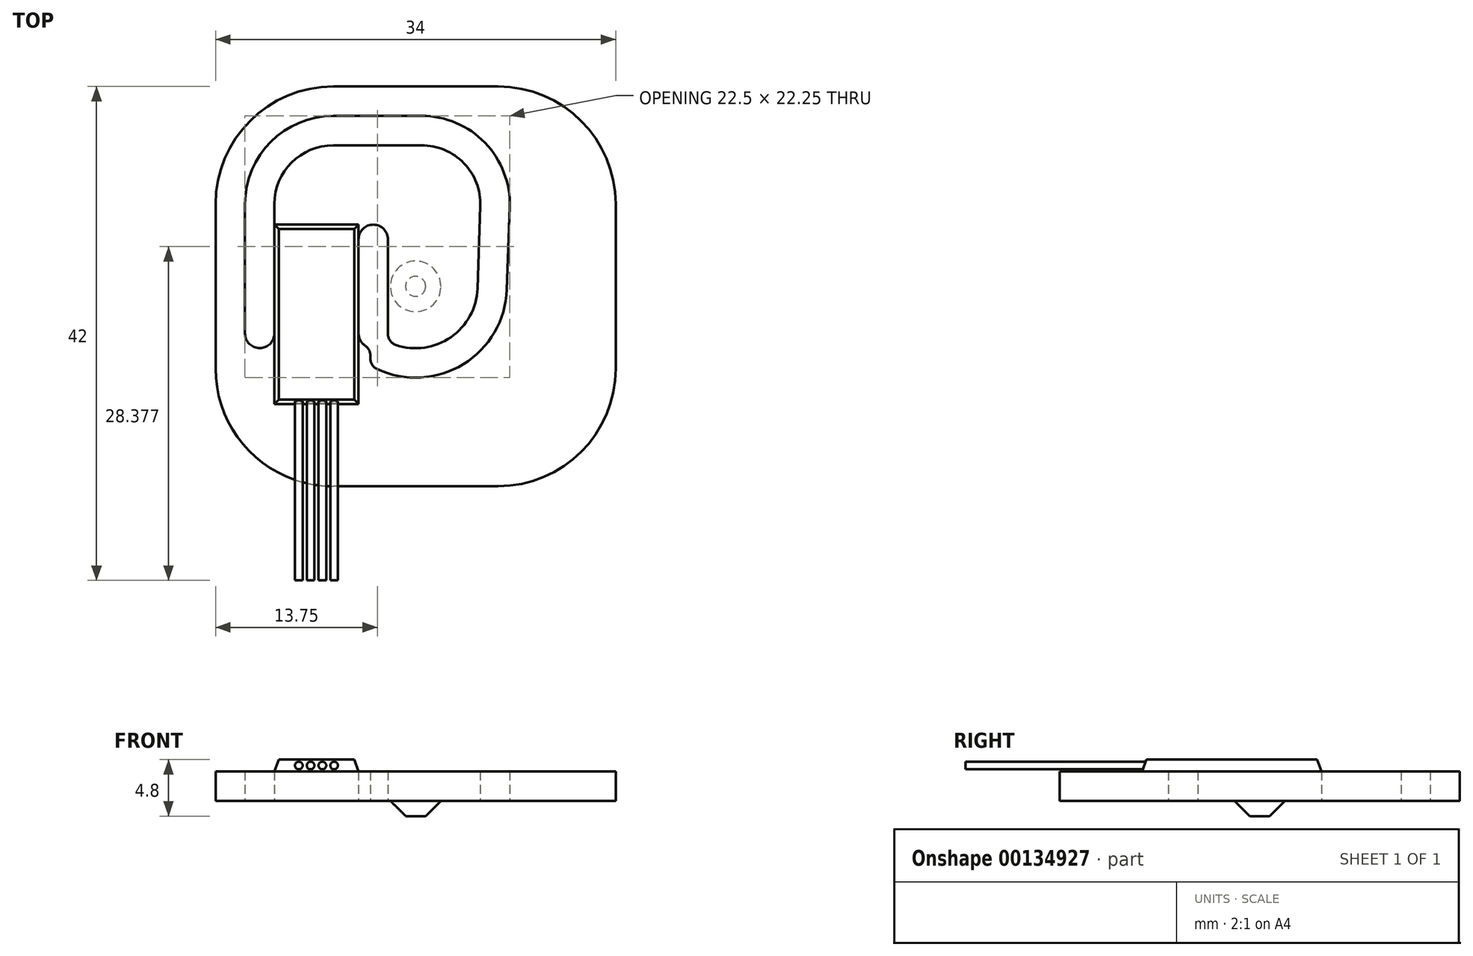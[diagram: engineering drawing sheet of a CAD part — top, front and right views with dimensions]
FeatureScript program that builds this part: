
annotation { "Feature Type Name" : "Feature", "Feature Type Description" : "" }
export const myFeature = defineFeature(function(context is Context, id is Id, definition is map)
    precondition{}
    {
        {
            var Q0;
            Q0=qCreatedBy(makeId("Top.planeOp"),FACE);
            var sketch = newSketch(context, id + "F0", { "sketchPlane" : qUnion([Q0])});
            skLineSegment(sketch, "E0.bottom", {"start": v(7, -17) * mm, "end": v(-7, -17) * mm});
            skLineSegment(sketch, "E0.top", {"start": v(7, 17) * mm, "end": v(-7, 17) * mm});
            skLineSegment(sketch, "E0.left", {"start": v(17, -7) * mm, "end": v(17, 7) * mm});
            skLineSegment(sketch, "E0.right", {"start": v(-17, -7) * mm, "end": v(-17, 7) * mm});
            skPoint(sketch, "E0.middle", {"position": v(0, 0) * mm});
            skPoint(sketch, "E1.visualSharp", {"position": v(-17, 17) * mm});
            skArc(sketch, "E1.filletArc", {"start": v(-7, 17) * mm, "mid": v(-14.07, 14.07) * mm, "end": v(-17, 7) * mm});
            skPoint(sketch, "E2.visualSharp", {"position": v(17, 17) * mm});
            skArc(sketch, "E2.filletArc", {"start": v(17, 7) * mm, "mid": v(14.07, 14.07) * mm, "end": v(7, 17) * mm});
            skPoint(sketch, "E3.visualSharp", {"position": v(17, -17) * mm});
            skArc(sketch, "E3.filletArc", {"start": v(7, -17) * mm, "mid": v(14.07, -14.07) * mm, "end": v(17, -7) * mm});
            skPoint(sketch, "E4.visualSharp", {"position": v(-17, -17) * mm});
            skArc(sketch, "E4.filletArc", {"start": v(-17, -7) * mm, "mid": v(-14.07, -14.07) * mm, "end": v(-7, -17) * mm});
            skLineSegment(sketch, "E5.0", {"start": v(0.5, 14.5) * mm, "end": v(-7, 14.5) * mm});
            skArc(sketch, "E5.1", {"start": v(-7, 14.5) * mm, "mid": v(-12.3, 12.3) * mm, "end": v(-14.5, 7) * mm});
            skLineSegment(sketch, "E5.2", {"start": v(-14.5, -4) * mm, "end": v(-14.5, 7) * mm});
            skArc(sketch, "E6", {"start": v(8, 6.74) * mm, "mid": v(5.9, 12.2) * mm, "end": v(0.5, 14.5) * mm});
            skLineSegment(sketch, "E7", {"start": v(8, 6.74) * mm, "end": v(7.76, -0.27) * mm});
            skArc(sketch, "E8", {"start": v(-3.27, -7.04) * mm, "mid": v(4.06, -6.61) * mm, "end": v(7.76, -0.27) * mm});
            skArc(sketch, "E9.0", {"start": v(-1.67, -4.99) * mm, "mid": v(3, -4.32) * mm, "end": v(5.26, -0.18) * mm});
            skLineSegment(sketch, "E9.1", {"start": v(5.5, 6.83) * mm, "end": v(5.26, -0.18) * mm});
            skLineSegment(sketch, "E9.2", {"start": v(-12, -4) * mm, "end": v(-12, 7) * mm});
            skArc(sketch, "E9.3", {"start": v(-7, 12) * mm, "mid": v(-10.54, 10.54) * mm, "end": v(-12, 7) * mm});
            skLineSegment(sketch, "E9.4", {"start": v(0.5, 12) * mm, "end": v(-7, 12) * mm});
            skArc(sketch, "E9.5", {"start": v(5.5, 6.83) * mm, "mid": v(4.1, 10.47) * mm, "end": v(0.5, 12) * mm});
            skArc(sketch, "E10", {"start": v(-14.5, -4) * mm, "mid": v(-13.25, -5.25) * mm, "end": v(-12, -4) * mm});
            skLineSegment(sketch, "E11", {"start": v(-2.35, -4.04) * mm, "end": v(-2.35, 4) * mm});
            skArc(sketch, "E12", {"start": v(-2.35, 4) * mm, "mid": v(-3.6, 5.25) * mm, "end": v(-4.85, 4) * mm});
            skLineSegment(sketch, "E13", {"start": v(-4.85, 4) * mm, "end": v(-4.85, -4) * mm});
            skArc(sketch, "E14", {"start": v(-4.85, -4) * mm, "mid": v(-4.7, -4.59) * mm, "end": v(-4.3, -5.04) * mm});
            skLineSegment(sketch, "E15", {"start": v(-3.85, -5.87) * mm, "end": v(-3.85, -6.13) * mm});
            skPoint(sketch, "E16.visualSharp", {"position": v(-3.85, -5.22) * mm});
            skArc(sketch, "E16.filletArc", {"start": v(-3.85, -5.87) * mm, "mid": v(-3.97, -5.4) * mm, "end": v(-4.3, -5.04) * mm});
            skPoint(sketch, "E17.visualSharp", {"position": v(-3.85, -6.74) * mm});
            skArc(sketch, "E17.filletArc", {"start": v(-3.85, -6.13) * mm, "mid": v(-3.7, -6.67) * mm, "end": v(-3.27, -7.04) * mm});
            skPoint(sketch, "E18.visualSharp", {"position": v(-2.35, -4.7) * mm});
            skArc(sketch, "E18.filletArc", {"start": v(-2.35, -4.04) * mm, "mid": v(-2.16, -4.62) * mm, "end": v(-1.67, -4.99) * mm});
            skSolve(sketch);
        }
        {
            var Q0;
            Q0 = qSketchRegion(id + "F0", true);
            extrude(context, id + "F1", {"entities" : qUnion([Q0]), "depth" : 2.5 * mm});
        }
        {
            var Q0;
            Q0=makeQuery(id+"F1.opExtrude","CAP_FACE",FACE,{"disambiguationData":[OSD([sQuery(id+"F0.wireOp",EDGE,"E0.bottom"),sQuery(id+"F0.wireOp",EDGE,"E0.top"),sQuery(id+"F0.wireOp",EDGE,"E0.left"),sQuery(id+"F0.wireOp",EDGE,"E0.right"),sQuery(id+"F0.wireOp",EDGE,"E1.filletArc"),sQuery(id+"F0.wireOp",EDGE,"E2.filletArc"),sQuery(id+"F0.wireOp",EDGE,"E3.filletArc"),sQuery(id+"F0.wireOp",EDGE,"E4.filletArc"),sQuery(id+"F0.wireOp",EDGE,"E5.0"),sQuery(id+"F0.wireOp",EDGE,"E5.1"),sQuery(id+"F0.wireOp",EDGE,"E5.2"),sQuery(id+"F0.wireOp",EDGE,"E6"),sQuery(id+"F0.wireOp",EDGE,"E7"),sQuery(id+"F0.wireOp",EDGE,"E8"),sQuery(id+"F0.wireOp",EDGE,"E9.0"),sQuery(id+"F0.wireOp",EDGE,"E9.1"),sQuery(id+"F0.wireOp",EDGE,"E9.2"),sQuery(id+"F0.wireOp",EDGE,"E9.3"),sQuery(id+"F0.wireOp",EDGE,"E9.4"),sQuery(id+"F0.wireOp",EDGE,"E9.5"),sQuery(id+"F0.wireOp",EDGE,"E10"),sQuery(id+"F0.wireOp",EDGE,"E11"),sQuery(id+"F0.wireOp",EDGE,"E12"),sQuery(id+"F0.wireOp",EDGE,"E13"),sQuery(id+"F0.wireOp",EDGE,"E14"),sQuery(id+"F0.wireOp",EDGE,"E15"),sQuery(id+"F0.wireOp",EDGE,"E16.filletArc"),sQuery(id+"F0.wireOp",EDGE,"E17.filletArc"),sQuery(id+"F0.wireOp",EDGE,"E18.filletArc")])],"isStart":false});
            var sketch = newSketch(context, id + "F2", { "sketchPlane" : qUnion([Q0])});
            skLineSegment(sketch, "E19.0", {"start": v(-12, -4) * mm, "end": v(-12, 5.25) * mm});
            skLineSegment(sketch, "E20.0", {"start": v(-4.85, 4) * mm, "end": v(-4.85, -4) * mm});
            skLineSegment(sketch, "E21", {"start": v(-4.85, 4) * mm, "end": v(-4.85, 5.25) * mm});
            skLineSegment(sketch, "E22", {"start": v(-4.85, 5.25) * mm, "end": v(-12, 5.25) * mm});
            skLineSegment(sketch, "E23", {"start": v(-12, -4) * mm, "end": v(-12, -10) * mm});
            skLineSegment(sketch, "E24", {"start": v(-12, -10) * mm, "end": v(-4.85, -10) * mm});
            skLineSegment(sketch, "E25", {"start": v(-4.85, -10) * mm, "end": v(-4.85, -4) * mm});
            skPoint(sketch, "E26.orphan", {"position": v(-12, 7) * mm});
            skSolve(sketch);
        }
        {
            var Q0;
            Q0 = qSketchRegion(id + "F2", true);
            extrude(context, id + "F3", {"entities" : qUnion([Q0]), "depth" : 1 * mm, "hasDraft" : true, "draftAngle" : 20 * degree, "draftPullDirection" : true});
        }
        {
            var Q0;
            Q0=qCreatedBy(makeId("Front.planeOp"),FACE);
            var sketch = newSketch(context, id + "F4", { "sketchPlane" : qUnion([Q0])});
            skLineSegment(sketch, "E27.0", {"start": v(-11.64, 3.5) * mm, "end": v(-5.21, 3.5) * mm, "construction": true});
            skLineSegment(sketch, "E28.0", {"start": v(-12, 2.5) * mm, "end": v(-4.85, 2.5) * mm, "construction": true});
            skCircle(sketch, "E29", {"center": v(-9.92, 3) * mm, "radius": 0.33 * mm});
            skCircle(sketch, "E30", {"center": v(-8.92, 3) * mm, "radius": 0.33 * mm});
            skCircle(sketch, "E31", {"center": v(-7.92, 3) * mm, "radius": 0.33 * mm});
            skCircle(sketch, "E32", {"center": v(-6.92, 3) * mm, "radius": 0.33 * mm});
            skLineSegment(sketch, "E33", {"start": v(-9.92, 3) * mm, "end": v(-8.92, 3) * mm, "construction": true});
            skLineSegment(sketch, "E34", {"start": v(-7.92, 3) * mm, "end": v(-6.92, 3) * mm, "construction": true});
            skLineSegment(sketch, "E35", {"start": v(-7.92, 3) * mm, "end": v(-8.92, 3) * mm, "construction": true});
            skLineSegment(sketch, "E36", {"start": v(-8.42, 3) * mm, "end": v(-8.42, 2.5) * mm, "construction": true});
            skPoint(sketch, "E37.orphan", {"position": v(-8.42, 3.5) * mm});
            skLineSegment(sketch, "E38", {"start": v(-8.42, 3) * mm, "end": v(-8.42, 3.5) * mm, "construction": true});
            skSolve(sketch);
        }
        {
            var Q0;
            Q0 = qSketchRegion(id + "F4", true);
            extrude(context, id + "F5", {"entities" : qUnion([Q0]), "operationType" : NewBodyOperationType.ADD, "depth" : 25 * mm});
        }
        {
            var Q0;
            Q0=makeQuery(id+"F1.opExtrude","CAP_FACE",FACE,{"disambiguationData":[OSD([sQuery(id+"F0.wireOp",EDGE,"E0.bottom"),sQuery(id+"F0.wireOp",EDGE,"E0.top"),sQuery(id+"F0.wireOp",EDGE,"E0.left"),sQuery(id+"F0.wireOp",EDGE,"E0.right"),sQuery(id+"F0.wireOp",EDGE,"E1.filletArc"),sQuery(id+"F0.wireOp",EDGE,"E2.filletArc"),sQuery(id+"F0.wireOp",EDGE,"E3.filletArc"),sQuery(id+"F0.wireOp",EDGE,"E4.filletArc"),sQuery(id+"F0.wireOp",EDGE,"E5.0"),sQuery(id+"F0.wireOp",EDGE,"E5.1"),sQuery(id+"F0.wireOp",EDGE,"E5.2"),sQuery(id+"F0.wireOp",EDGE,"E6"),sQuery(id+"F0.wireOp",EDGE,"E7"),sQuery(id+"F0.wireOp",EDGE,"E8"),sQuery(id+"F0.wireOp",EDGE,"E9.0"),sQuery(id+"F0.wireOp",EDGE,"E9.1"),sQuery(id+"F0.wireOp",EDGE,"E9.2"),sQuery(id+"F0.wireOp",EDGE,"E9.3"),sQuery(id+"F0.wireOp",EDGE,"E9.4"),sQuery(id+"F0.wireOp",EDGE,"E9.5"),sQuery(id+"F0.wireOp",EDGE,"E10"),sQuery(id+"F0.wireOp",EDGE,"E11"),sQuery(id+"F0.wireOp",EDGE,"E12"),sQuery(id+"F0.wireOp",EDGE,"E13"),sQuery(id+"F0.wireOp",EDGE,"E14"),sQuery(id+"F0.wireOp",EDGE,"E15"),sQuery(id+"F0.wireOp",EDGE,"E16.filletArc"),sQuery(id+"F0.wireOp",EDGE,"E17.filletArc"),sQuery(id+"F0.wireOp",EDGE,"E18.filletArc")])],"isStart":true});
            var sketch = newSketch(context, id + "F6", { "sketchPlane" : qUnion([Q0])});
            skCircle(sketch, "E39", {"center": v(0, 0) * mm, "radius": 2.15 * mm});
            skSolve(sketch);
        }
        {
            var Q0;
            Q0 = qSketchRegion(id + "F6", true);
            extrude(context, id + "F7", {"entities" : qUnion([Q0]), "operationType" : NewBodyOperationType.ADD, "depth" : (3.8 - 2.5) * mm, "hasDraft" : true, "draftAngle" : 45 * degree, "draftPullDirection" : true});
        }
    });
